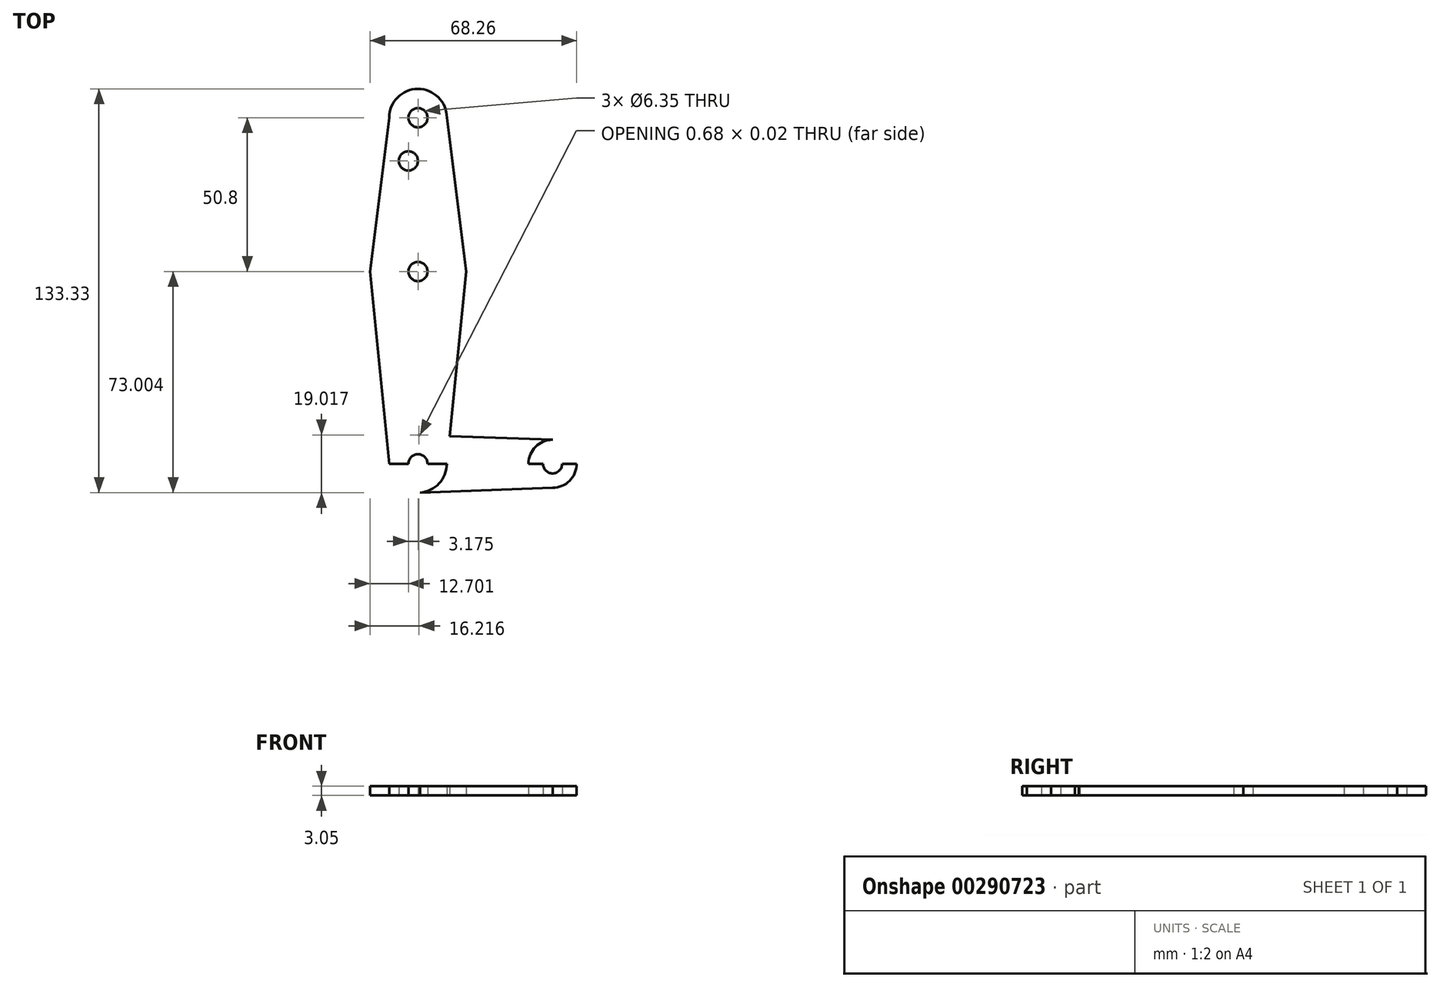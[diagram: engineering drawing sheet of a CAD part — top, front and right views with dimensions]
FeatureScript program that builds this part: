
annotation { "Feature Type Name" : "Feature", "Feature Type Description" : "" }
export const myFeature = defineFeature(function(context is Context, id is Id, definition is map)
    precondition{}
    {
        {
            var Q0;
            Q0=qCreatedBy(makeId("Top.planeOp"),FACE);
            var sketch = newSketch(context, id + "F0", { "sketchPlane" : qUnion([Q0])});
            skCircle(sketch, "E0", {"center": v(-26.64, 68.77) * mm, "radius": 9.53 * mm});
            skCircle(sketch, "E1", {"center": v(-26.64, -45.53) * mm, "radius": 9.53 * mm});
            skCircle(sketch, "E2", {"center": v(17.8, -45.53) * mm, "radius": 7.94 * mm});
            skCircle(sketch, "E3", {"center": v(-26.64, 17.97) * mm, "radius": 15.88 * mm});
            skLineSegment(sketch, "E4", {"start": v(-26.64, -45.53) * mm, "end": v(17.8, -45.53) * mm, "construction": true});
            skLineSegment(sketch, "E5", {"start": v(-26.64, -45.53) * mm, "end": v(-36.17, -45.53) * mm, "construction": true});
            skLineSegment(sketch, "E6", {"start": v(-36.17, -45.53) * mm, "end": v(-26.64, -45.53) * mm});
            skLineSegment(sketch, "E7", {"start": v(-17.12, -45.53) * mm, "end": v(-26.64, -45.53) * mm});
            skLineSegment(sketch, "E8", {"start": v(-26.64, -45.53) * mm, "end": v(-26.64, -36) * mm});
            skLineSegment(sketch, "E9", {"start": v(-26.64, -36) * mm, "end": v(-26.64, -55.05) * mm, "construction": true});
            skLineSegment(sketch, "E10", {"start": v(17.8, -45.53) * mm, "end": v(25.74, -45.53) * mm});
            skLineSegment(sketch, "E11", {"start": v(25.74, -45.53) * mm, "end": v(17.8, -45.53) * mm, "construction": true});
            skLineSegment(sketch, "E12", {"start": v(9.87, -45.53) * mm, "end": v(25.74, -45.53) * mm});
            skLineSegment(sketch, "E13", {"start": v(17.8, -45.53) * mm, "end": v(17.8, -53.46) * mm, "construction": true});
            skLineSegment(sketch, "E14", {"start": v(17.8, -37.59) * mm, "end": v(17.8, -45.53) * mm, "construction": true});
            skLineSegment(sketch, "E15", {"start": v(-26.64, 78.3) * mm, "end": v(-26.64, 68.77) * mm, "construction": true});
            skLineSegment(sketch, "E16", {"start": v(-36.17, 68.77) * mm, "end": v(-42.52, 17.97) * mm});
            skLineSegment(sketch, "E17", {"start": v(-42.52, 17.97) * mm, "end": v(-36.17, -45.53) * mm});
            skLineSegment(sketch, "E18", {"start": v(-17.12, 68.77) * mm, "end": v(-10.77, 17.97) * mm});
            skLineSegment(sketch, "E19", {"start": v(-10.77, 17.97) * mm, "end": v(-17.12, -45.53) * mm});
            skLineSegment(sketch, "E20", {"start": v(-26.64, -36) * mm, "end": v(17.8, -37.59) * mm});
            skLineSegment(sketch, "E21", {"start": v(-26.64, -55.05) * mm, "end": v(17.8, -53.46) * mm});
            skLineSegment(sketch, "E22", {"start": v(-26.64, 68.77) * mm, "end": v(-26.64, -45.53) * mm, "construction": true});
            skLineSegment(sketch, "E23", {"start": v(-10.77, 17.97) * mm, "end": v(16.41, 17.97) * mm, "construction": true});
            skLineSegment(sketch, "E24", {"start": v(16.41, 17.97) * mm, "end": v(16.41, 54.5) * mm, "construction": true});
            skLineSegment(sketch, "E25", {"start": v(16.41, 54.5) * mm, "end": v(-29.82, 54.5) * mm});
            skCircle(sketch, "E26", {"center": v(-29.82, 54.5) * mm, "radius": 3.18 * mm});
            skCircle(sketch, "E27", {"center": v(-26.64, 68.77) * mm, "radius": 3.18 * mm});
            skCircle(sketch, "E28", {"center": v(-26.64, 17.97) * mm, "radius": 3.18 * mm});
            skCircle(sketch, "E29", {"center": v(-26.64, -45.53) * mm, "radius": 3.18 * mm});
            skCircle(sketch, "E30", {"center": v(17.8, -45.53) * mm, "radius": 3.18 * mm});
            skSolve(sketch);
        }
        {
            var Q0;
            Q0=makeQuery(id+"F0.imprint","IMPRINT",FACE,{"disambiguationData":[TD([[makeQuery(id+"F0.imprint","IMPRINT",EDGE,{"derivedFrom":sQuery(id+"F0.wireOp",EDGE,"E26")}),-1.0]])]});
            var Q1;
            Q1=makeQuery(id+"F0.imprint","IMPRINT",FACE,{"disambiguationData":[TD([[makeQuery(id+"F0.imprint","IMPRINT",EDGE,{"derivedFrom":sQuery(id+"F0.wireOp",EDGE,"E27")}),-1.0]])]});
            var Q2;
            Q2=makeQuery(id+"F0.imprint","IMPRINT",FACE,{"disambiguationData":[TD([[makeQuery(id+"F0.imprint","IMPRINT",EDGE,{"derivedFrom":sQuery(id+"F0.wireOp",EDGE,"E28")}),-1.0]])]});
            var Q3;
            {var subQ0=sQuery(id+"F0.wireOp",EDGE,"E17");var subQ3=sQuery(id+"F0.wireOp",EDGE,"E3");var subQ4=makeQuery(id+"F0.imprint","INTERSECT",VERTEX,{"derivedFrom":[subQ3,subQ0]});Q3=makeQuery(id+"F0.imprint","IMPRINT",FACE,{"disambiguationData":[TD([[makeQuery(id+"F0.imprint","IMPRINT",EDGE,{"disambiguationData":[TD([[subQ4,-1.0]])],"derivedFrom":subQ3}),-1.0]])]});}
            var Q4;
            {var subQ0=sQuery(id+"F0.wireOp",EDGE,"E6");var subQ5=sQuery(id+"F0.wireOp",EDGE,"E29");var subQ6=makeQuery(id+"F0.imprint","INTERSECT",VERTEX,{"derivedFrom":[subQ0,subQ5]});Q4=makeQuery(id+"F0.imprint","IMPRINT",FACE,{"disambiguationData":[TD([[makeQuery(id+"F0.imprint","IMPRINT",EDGE,{"disambiguationData":[TD([[subQ6,1.0]])],"derivedFrom":subQ5}),-1.0]])]});}
            var Q5;
            {var subQ4=sQuery(id+"F0.wireOp",EDGE,"E29");var subQ6=sQuery(id+"F0.wireOp",EDGE,"E7");var subQ7=makeQuery(id+"F0.imprint","INTERSECT",VERTEX,{"derivedFrom":[subQ6,subQ4]});Q5=makeQuery(id+"F0.imprint","IMPRINT",FACE,{"disambiguationData":[TD([[makeQuery(id+"F0.imprint","IMPRINT",EDGE,{"disambiguationData":[TD([[subQ7,-1.0]])],"derivedFrom":subQ4}),-1.0]])]});}
            var Q6;
            {var subQ1=sQuery(id+"F0.wireOp",EDGE,"E1");var subQ7=sQuery(id+"F0.wireOp",EDGE,"E21");var subQ9=makeQuery(id+"F0.imprint","INTERSECT",VERTEX,{"disambiguationData":[OD(0.0)],"derivedFrom":[subQ1,subQ7]});Q6=makeQuery(id+"F0.imprint","IMPRINT",FACE,{"disambiguationData":[TD([[makeQuery(id+"F0.imprint","IMPRINT",EDGE,{"disambiguationData":[TD([[subQ9,-1.0]])],"derivedFrom":subQ7}),1.0]])]});}
            var Q7;
            {var subQ1=sQuery(id+"F0.wireOp",EDGE,"E1");var subQ7=sQuery(id+"F0.wireOp",EDGE,"E21");var subQ9=makeQuery(id+"F0.imprint","INTERSECT",VERTEX,{"disambiguationData":[OD(0.0)],"derivedFrom":[subQ1,subQ7]});Q7=makeQuery(id+"F0.imprint","IMPRINT",FACE,{"disambiguationData":[TD([[makeQuery(id+"F0.imprint","IMPRINT",EDGE,{"disambiguationData":[TD([[subQ9,-1.0]])],"derivedFrom":subQ7}),1.0]])]});}
            var Q8;
            {var subQ0=sQuery(id+"F0.wireOp",EDGE,"E19");var subQ3=sQuery(id+"F0.wireOp",EDGE,"E20");var subQ5=makeQuery(id+"F0.imprint","INTERSECT",VERTEX,{"derivedFrom":[subQ0,subQ3]});Q8=makeQuery(id+"F0.imprint","IMPRINT",FACE,{"disambiguationData":[TD([[makeQuery(id+"F0.imprint","IMPRINT",EDGE,{"disambiguationData":[TD([[subQ5,1.0]])],"derivedFrom":subQ3}),-1.0]])]});}
            var Q9;
            {var subQ0=sQuery(id+"F0.wireOp",EDGE,"E12");var subQ1=sQuery(id+"F0.wireOp",EDGE,"E2");var subQ2=makeQuery(id+"F0.imprint","INTERSECT",VERTEX,{"disambiguationData":[OD(1.0)],"derivedFrom":[subQ1,subQ0]});Q9=makeQuery(id+"F0.imprint","IMPRINT",FACE,{"disambiguationData":[TD([[makeQuery(id+"F0.imprint","IMPRINT",EDGE,{"disambiguationData":[TD([[subQ2,-1.0]])],"derivedFrom":subQ1}),1.0]])]});}
            var Q10;
            {var subQ0=sQuery(id+"F0.wireOp",EDGE,"E12");var subQ1=sQuery(id+"F0.wireOp",EDGE,"E2");var subQ6=makeQuery(id+"F0.imprint","INTERSECT",VERTEX,{"disambiguationData":[OD(0.0)],"derivedFrom":[subQ1,subQ0]});Q10=makeQuery(id+"F0.imprint","IMPRINT",FACE,{"disambiguationData":[TD([[makeQuery(id+"F0.imprint","IMPRINT",EDGE,{"disambiguationData":[TD([[subQ6,-1.0]])],"derivedFrom":subQ1}),1.0]])]});}
            var Q11;
            {var subQ5=sQuery(id+"F0.wireOp",EDGE,"E2");var subQ6=makeQuery(id+"F0.imprint","INTERSECT",VERTEX,{"disambiguationData":[OD(0.0)],"derivedFrom":[subQ5,sQuery(id+"F0.wireOp",EDGE,"E12")]});Q11=makeQuery(id+"F0.imprint","IMPRINT",FACE,{"disambiguationData":[TD([[makeQuery(id+"F0.imprint","IMPRINT",EDGE,{"disambiguationData":[TD([[subQ6,1.0]])],"derivedFrom":subQ5}),-1.0]])]});}
            extrude(context, id + "F1", {"entities" : qUnion([Q0, Q1, Q2, Q3, Q4, Q5, Q6, Q7, Q8, Q9, Q10, Q11]), "depth" : 3.05 * mm});
        }
    });
